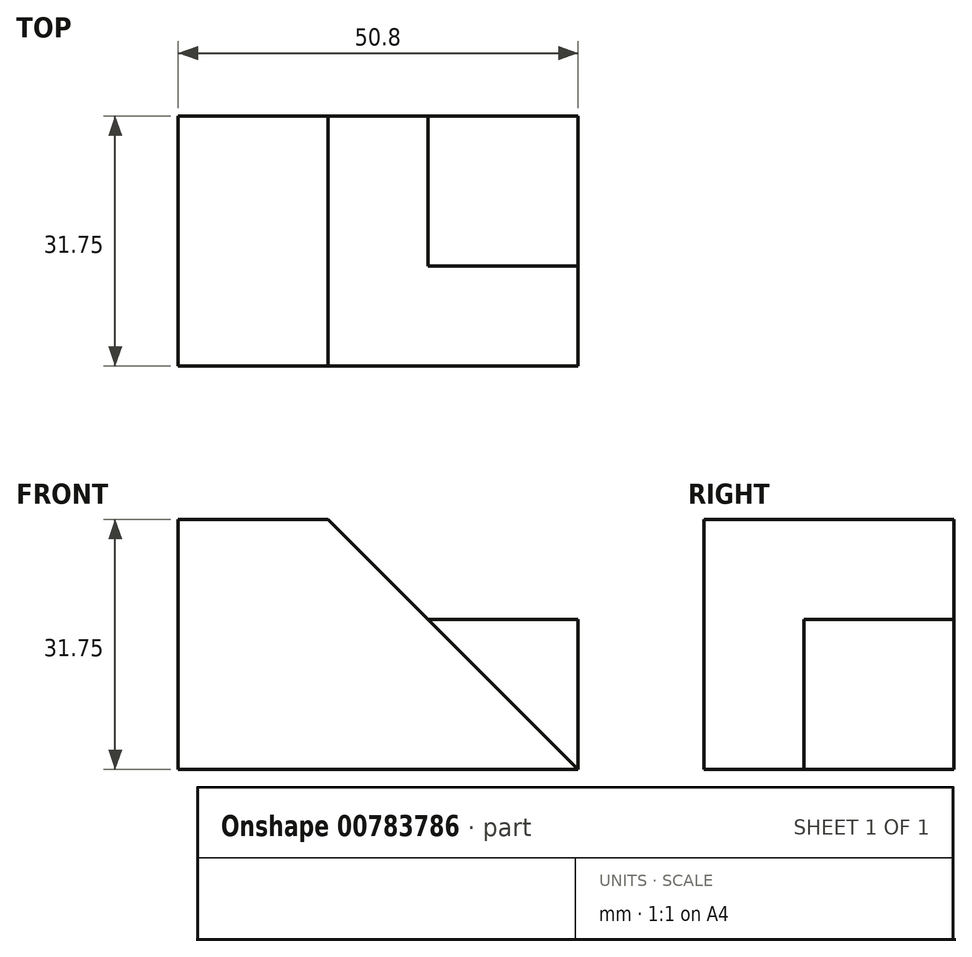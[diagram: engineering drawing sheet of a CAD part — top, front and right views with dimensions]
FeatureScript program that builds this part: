
annotation { "Feature Type Name" : "Feature", "Feature Type Description" : "" }
export const myFeature = defineFeature(function(context is Context, id is Id, definition is map)
    precondition{}
    {
        {
            var Q0;
            Q0=qCreatedBy(makeId("Front.planeOp"),FACE);
            var sketch = newSketch(context, id + "F0", { "sketchPlane" : qUnion([Q0])});
            skLineSegment(sketch, "E0", {"start": v(0, 0) * mm, "end": v(50.8, 0) * mm});
            skLineSegment(sketch, "E1", {"start": v(0, 0) * mm, "end": v(0, 31.75) * mm});
            skLineSegment(sketch, "E2", {"start": v(0, 31.75) * mm, "end": v(50.8, 31.75) * mm});
            skLineSegment(sketch, "E3", {"start": v(50.8, 31.75) * mm, "end": v(50.8, 0) * mm});
            skSolve(sketch);
        }
        {
            var Q0;
            Q0=makeQuery(id+"F0.imprint","IMPRINT",FACE,{"disambiguationData":[TD([[makeQuery(id+"F0.imprint","IMPRINT",EDGE,{"derivedFrom":sQuery(id+"F0.wireOp",EDGE,"E0")}),1.0]])]});
            extrude(context, id + "F1", {"entities" : qUnion([Q0]), "depth" : 31.75 * mm, "offsetDistance" : 25.4 * mm});
        }
        {
            var Q0;
            Q0=makeQuery(id+"F1.opExtrude","CAP_FACE",FACE,{"disambiguationData":[OSD([sQuery(id+"F0.wireOp",EDGE,"E0"),sQuery(id+"F0.wireOp",EDGE,"E1"),sQuery(id+"F0.wireOp",EDGE,"E2"),sQuery(id+"F0.wireOp",EDGE,"E3")])],"isStart":false});
            var sketch = newSketch(context, id + "F2", { "sketchPlane" : qUnion([Q0])});
            skLineSegment(sketch, "E4", {"start": v(0, 31.75) * mm, "end": v(19.05, 31.75) * mm});
            skLineSegment(sketch, "E5", {"start": v(50.8, 0) * mm, "end": v(50.8, 19.05) * mm});
            skLineSegment(sketch, "E6", {"start": v(50.8, 19.05) * mm, "end": v(31.75, 19.05) * mm});
            skLineSegment(sketch, "E7", {"start": v(19.05, 31.75) * mm, "end": v(31.75, 19.05) * mm});
            skSolve(sketch);
        }
        {
            var Q0;
            {var subQ0=sQuery(id+"F2.wireOp",EDGE,"E6");Q0=makeQuery(id+"F2.imprint","IMPRINT",FACE,{"disambiguationData":[TD([[makeQuery(id+"F2.imprint","IMPRINT",EDGE,{"derivedFrom":subQ0}),-1.0]])]});}
            extrude(context, id + "F3", {"entities" : qUnion([Q0]), "operationType" : NewBodyOperationType.REMOVE, "oppositeDirection" : true, "depth" : 31.75 * mm, "offsetDistance" : 25.4 * mm});
        }
        {
            var Q0;
            Q0=makeQuery(id+"F1.opExtrude","CAP_FACE",FACE,{"disambiguationData":[OSD([sQuery(id+"F0.wireOp",EDGE,"E0"),sQuery(id+"F0.wireOp",EDGE,"E1"),sQuery(id+"F0.wireOp",EDGE,"E2"),sQuery(id+"F0.wireOp",EDGE,"E3")])],"isStart":false});
            var sketch = newSketch(context, id + "F4", { "sketchPlane" : qUnion([Q0])});
            skLineSegment(sketch, "E8", {"start": v(31.75, 19.05) * mm, "end": v(50.8, 0) * mm});
            skSolve(sketch);
        }
        {
            var Q0;
            Q0=makeQuery(id+"F4.imprint","IMPRINT",FACE,{"disambiguationData":[TD([[makeQuery(id+"F4.imprint","IMPRINT",EDGE,{"derivedFrom":sQuery(id+"F4.wireOp",EDGE,"E8")}),1.0]])]});
            extrude(context, id + "F5", {"entities" : qUnion([Q0]), "operationType" : NewBodyOperationType.REMOVE, "oppositeDirection" : true, "depth" : 12.7 * mm, "offsetDistance" : 25.4 * mm});
        }
    });
